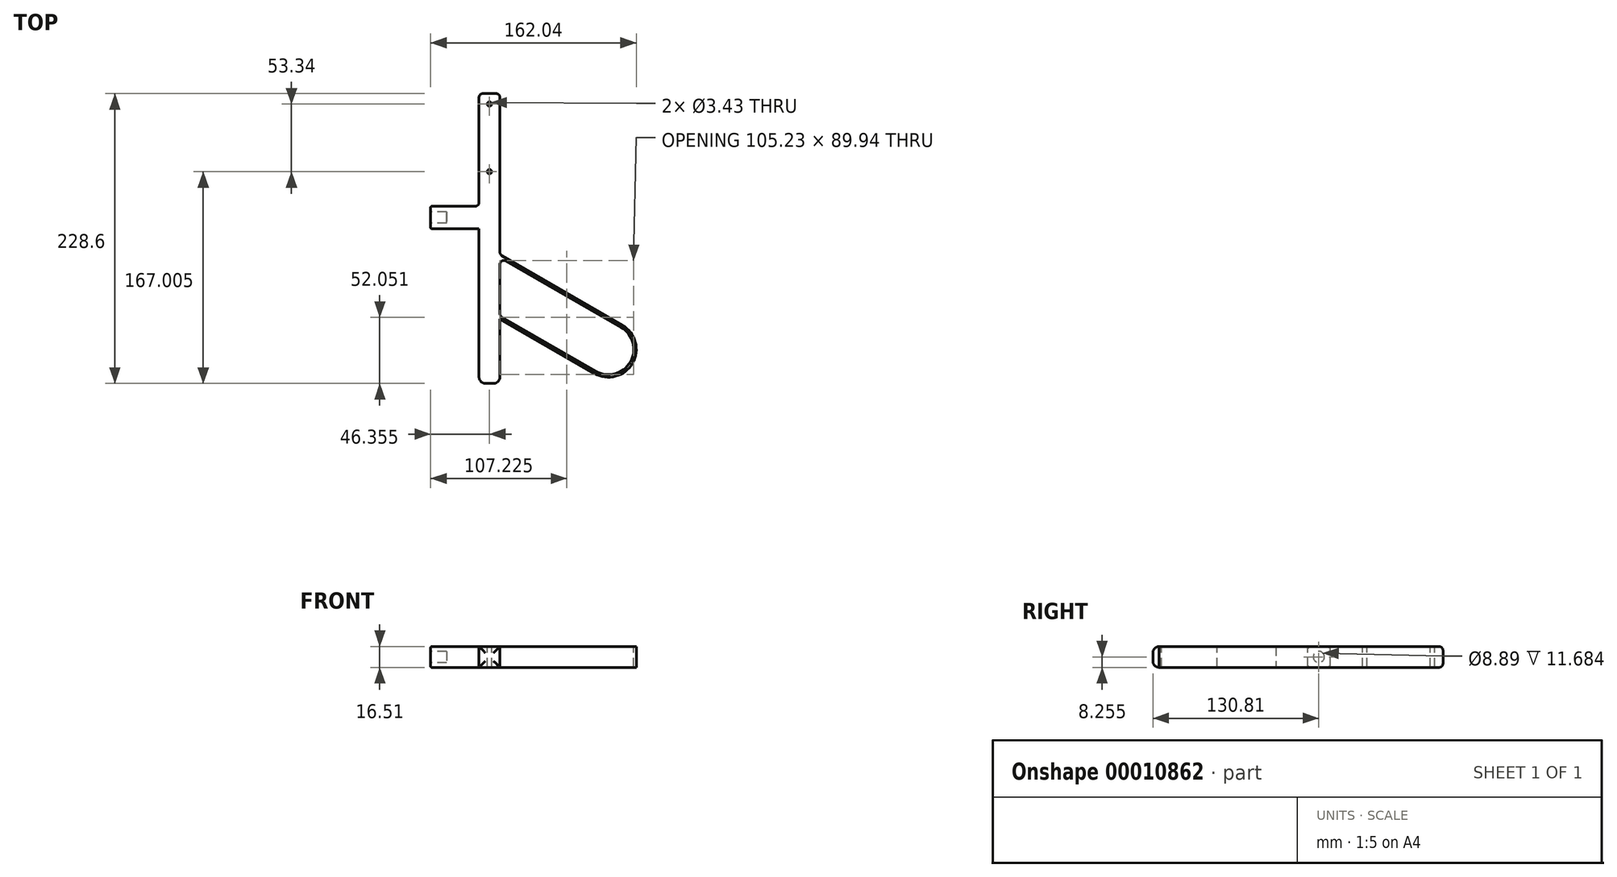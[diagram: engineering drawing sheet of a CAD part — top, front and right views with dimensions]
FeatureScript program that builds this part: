
annotation { "Feature Type Name" : "Feature", "Feature Type Description" : "" }
export const myFeature = defineFeature(function(context is Context, id is Id, definition is map)
    precondition{}
    {
        {
            var Q0;
            Q0=qCreatedBy(makeId("Top.planeOp"),FACE);
            var sketch = newSketch(context, id + "F0", { "sketchPlane" : qUnion([Q0])});
            skLineSegment(sketch, "E0.bottom", {"start": v(0, 0) * mm, "end": v(16.51, 0) * mm});
            skLineSegment(sketch, "E0.top", {"start": v(0, 228.6) * mm, "end": v(16.5, 228.6) * mm});
            skLineSegment(sketch, "E0.left", {"start": v(0, 0) * mm, "end": v(0, 228.6) * mm});
            skLineSegment(sketch, "E0.right", {"start": v(16.51, 0) * mm, "end": v(16.5, 228.6) * mm});
            skSolve(sketch);
        }
        {
            var Q0;
            Q0 = qSketchRegion(id + "F0", true);
            extrude(context, id + "F1", {"entities" : qUnion([Q0]), "depth" : 16.5 * mm});
        }
        {
            var Q0;
            Q0=makeQuery(id+"F1.opExtrude","CAP_FACE",FACE,{"disambiguationData":[OSD([sQuery(id+"F0.wireOp",EDGE,"E0.bottom"),sQuery(id+"F0.wireOp",EDGE,"E0.top"),sQuery(id+"F0.wireOp",EDGE,"E0.left"),sQuery(id+"F0.wireOp",EDGE,"E0.right")])],"isStart":false});
            var sketch = newSketch(context, id + "F2", { "sketchPlane" : qUnion([Q0])});
            skCircle(sketch, "E1", {"center": v(8.25, 220.35) * mm, "radius": 1.71 * mm});
            skPoint(sketch, "E1.centerSnap0", {"position": v(8.25, 228.6) * mm});
            skCircle(sketch, "E2", {"center": v(8.25, 167) * mm, "radius": 1.71 * mm});
            skLineSegment(sketch, "E3", {"start": v(8.25, 228.6) * mm, "end": v(8.25, 220.35) * mm});
            skLineSegment(sketch, "E4", {"start": v(8.25, 228.6) * mm, "end": v(0, 228.6) * mm});
            skLineSegment(sketch, "E5", {"start": v(16.5, 101.6) * mm, "end": v(132, 34.93) * mm});
            skLineSegment(sketch, "E6", {"start": v(16.5, 50.8) * mm, "end": v(110, -3.17) * mm});
            skLineSegment(sketch, "E7", {"start": v(132, 34.93) * mm, "end": v(110, -3.17) * mm});
            skArc(sketch, "E8", {"start": v(90.95, 7.82) * mm, "mid": v(121, 15.88) * mm, "end": v(112.94, 45.92) * mm});
            skLineSegment(sketch, "E9", {"start": v(0, 139.7) * mm, "end": v(-38.1, 139.7) * mm});
            skLineSegment(sketch, "E10", {"start": v(0, 121.92) * mm, "end": v(-38.1, 121.92) * mm});
            skLineSegment(sketch, "E11", {"start": v(-38.1, 139.7) * mm, "end": v(-38.1, 121.92) * mm});
            skArc(sketch, "E12", {"start": v(91.96, 9.58) * mm, "mid": v(119.24, 16.9) * mm, "end": v(111.93, 44.16) * mm});
            skLineSegment(sketch, "E13", {"start": v(111.93, 44.16) * mm, "end": v(16.5, 99.25) * mm});
            skLineSegment(sketch, "E14", {"start": v(91.96, 9.58) * mm, "end": v(16.5, 53.15) * mm});
            skSolve(sketch);
        }
        {
            var Q0;
            {var subQ1=makeQuery(id+"F1.opExtrude","CAP_EDGE",EDGE,{"disambiguationData":[OSD([sQuery(id+"F0.wireOp",EDGE,"E0.right")])],"isStart":false});var subQ5=sQuery(id+"F2.wireOp",EDGE,"E5");var subQ8=makeQuery(id+"F2.imprint","INTERSECT",VERTEX,{"derivedFrom":[subQ1,subQ5]});Q0=makeQuery(id+"F2.imprint","IMPRINT",FACE,{"disambiguationData":[TD([[makeQuery(id+"F2.imprint","IMPRINT",EDGE,{"disambiguationData":[TD([[subQ8,-1.0]])],"derivedFrom":subQ5}),-1.0]])]});}
            var Q1;
            Q1=makeQuery(id+"F1.opExtrude","CAP_FACE",FACE,{"disambiguationData":[OSD([sQuery(id+"F0.wireOp",EDGE,"E0.bottom"),sQuery(id+"F0.wireOp",EDGE,"E0.top"),sQuery(id+"F0.wireOp",EDGE,"E0.left"),sQuery(id+"F0.wireOp",EDGE,"E0.right")])],"isStart":true});
            extrude(context, id + "F3", {"entities" : qUnion([Q0]), "operationType" : NewBodyOperationType.ADD, "endBound" : BoundingType.UP_TO_SURFACE, "oppositeDirection" : true, "endBoundEntityFace" : qUnion([Q1]), "depth" : 25.4 * mm});
        }
        {
            var Q0;
            Q0=makeQuery(id+"F2.imprint","IMPRINT",FACE,{"disambiguationData":[TD([[makeQuery(id+"F2.imprint","IMPRINT",EDGE,{"derivedFrom":sQuery(id+"F2.wireOp",EDGE,"E1")}),1.0]])]});
            var Q1;
            Q1=makeQuery(id+"F2.imprint","IMPRINT",FACE,{"disambiguationData":[TD([[makeQuery(id+"F2.imprint","IMPRINT",EDGE,{"derivedFrom":sQuery(id+"F2.wireOp",EDGE,"E2")}),1.0]])]});
            extrude(context, id + "F4", {"entities" : qUnion([Q0, Q1]), "operationType" : NewBodyOperationType.REMOVE, "endBound" : BoundingType.UP_TO_NEXT, "oppositeDirection" : true, "depth" : 25.4 * mm});
        }
        {
            var Q0;
            {var subQ0=sQuery(id+"F2.wireOp",EDGE,"E9");Q0=makeQuery(id+"F2.imprint","IMPRINT",FACE,{"disambiguationData":[TD([[makeQuery(id+"F2.imprint","IMPRINT",EDGE,{"derivedFrom":subQ0}),1.0]])]});}
            var Q1;
            Q1=makeQuery(id+"F1.opExtrude","CAP_FACE",FACE,{"disambiguationData":[OSD([sQuery(id+"F0.wireOp",EDGE,"E0.bottom"),sQuery(id+"F0.wireOp",EDGE,"E0.top"),sQuery(id+"F0.wireOp",EDGE,"E0.left"),sQuery(id+"F0.wireOp",EDGE,"E0.right")])],"isStart":true});
            extrude(context, id + "F5", {"entities" : qUnion([Q0]), "operationType" : NewBodyOperationType.ADD, "endBound" : BoundingType.UP_TO_SURFACE, "oppositeDirection" : true, "endBoundEntityFace" : qUnion([Q1]), "depth" : 25.4 * mm});
        }
        {
            var Q0;
            Q0=makeQuery(id+"F5.opExtrude","SWEPT_FACE",FACE,{"disambiguationData":[OSD([sQuery(id+"F2.wireOp",EDGE,"E11")])]});
            var sketch = newSketch(context, id + "F6", { "sketchPlane" : qUnion([Q0])});
            skCircle(sketch, "E15", {"center": v(-130.8, 8.25) * mm, "radius": 4.45 * mm});
            skPoint(sketch, "E15.centerSnap0", {"position": v(-130.8, 16.51) * mm});
            skPoint(sketch, "E15.centerSnap1", {"position": v(-139.7, 8.25) * mm});
            skSolve(sketch);
        }
        {
            var Q0;
            Q0=makeQuery(id+"F6.imprint","IMPRINT",FACE,{"disambiguationData":[TD([[makeQuery(id+"F6.imprint","IMPRINT",EDGE,{"derivedFrom":sQuery(id+"F6.wireOp",EDGE,"E15")}),1.0]])]});
            extrude(context, id + "F7", {"entities" : qUnion([Q0]), "operationType" : NewBodyOperationType.REMOVE, "oppositeDirection" : true, "depth" : 12.7 * mm});
        }
        {
            var Q0;
            Q0=makeQuery(id+"F1.opExtrude","SWEPT_FACE",FACE,{"disambiguationData":[OSD([sQuery(id+"F0.wireOp",EDGE,"E0.bottom")])]});
            fillet(context, id + "F8", {"entities" : qUnion([Q0]), "radius" : 5.08 * mm, "tangentPropagation" : true, "allowEdgeOverflow" : false});
        }
        {
            var Q0;
            Q0=makeQuery(id+"F3.opExtrude","SWEPT_EDGE",EDGE,{"disambiguationData":[OSD([sQuery(id+"F0.wireOp",EDGE,"E0.right"),sQuery(id+"F2.wireOp",EDGE,"E5")])]});
            var Q1;
            Q1=makeQuery(id+"F3.opExtrude","SWEPT_EDGE",EDGE,{"disambiguationData":[OSD([sQuery(id+"F0.wireOp",EDGE,"E0.right"),sQuery(id+"F2.wireOp",EDGE,"E6")])]});
            var Q2;
            Q2=makeQuery(id+"F5.opExtrude","SWEPT_EDGE",EDGE,{"disambiguationData":[OSD([sQuery(id+"F0.wireOp",EDGE,"E0.left"),sQuery(id+"F2.wireOp",EDGE,"E10")])]});
            var Q3;
            Q3=makeQuery(id+"F5.opExtrude","SWEPT_EDGE",EDGE,{"disambiguationData":[OSD([sQuery(id+"F0.wireOp",EDGE,"E0.left"),sQuery(id+"F2.wireOp",EDGE,"E9")])]});
            var Q4;
            Q4=makeQuery(id+"F3.opExtrude","SWEPT_EDGE",EDGE,{"disambiguationData":[OSD([sQuery(id+"F0.wireOp",EDGE,"E0.right"),sQuery(id+"F2.wireOp",EDGE,"E13")])]});
            var Q5;
            Q5=makeQuery(id+"F3.opExtrude","SWEPT_EDGE",EDGE,{"disambiguationData":[OSD([sQuery(id+"F0.wireOp",EDGE,"E0.right"),sQuery(id+"F2.wireOp",EDGE,"E14")])]});
            var Q6;
            Q6=makeQuery(id+"F1.opExtrude","SWEPT_FACE",FACE,{"disambiguationData":[OSD([sQuery(id+"F0.wireOp",EDGE,"E0.top")])]});
            fillet(context, id + "F9", {"entities" : qUnion([Q0, Q1, Q2, Q3, Q4, Q5, Q6]), "radius" : 3.05 * mm, "tangentPropagation" : true, "allowEdgeOverflow" : false});
        }
        {
            var Q0;
            Q0=makeQuery(id+"F5.opExtrude","SWEPT_FACE",FACE,{"disambiguationData":[OSD([sQuery(id+"F2.wireOp",EDGE,"E11")])]});
            fillet(context, id + "F10", {"entities" : qUnion([Q0]), "radius" : 1.02 * mm, "tangentPropagation" : true, "allowEdgeOverflow" : false});
        }
    });
